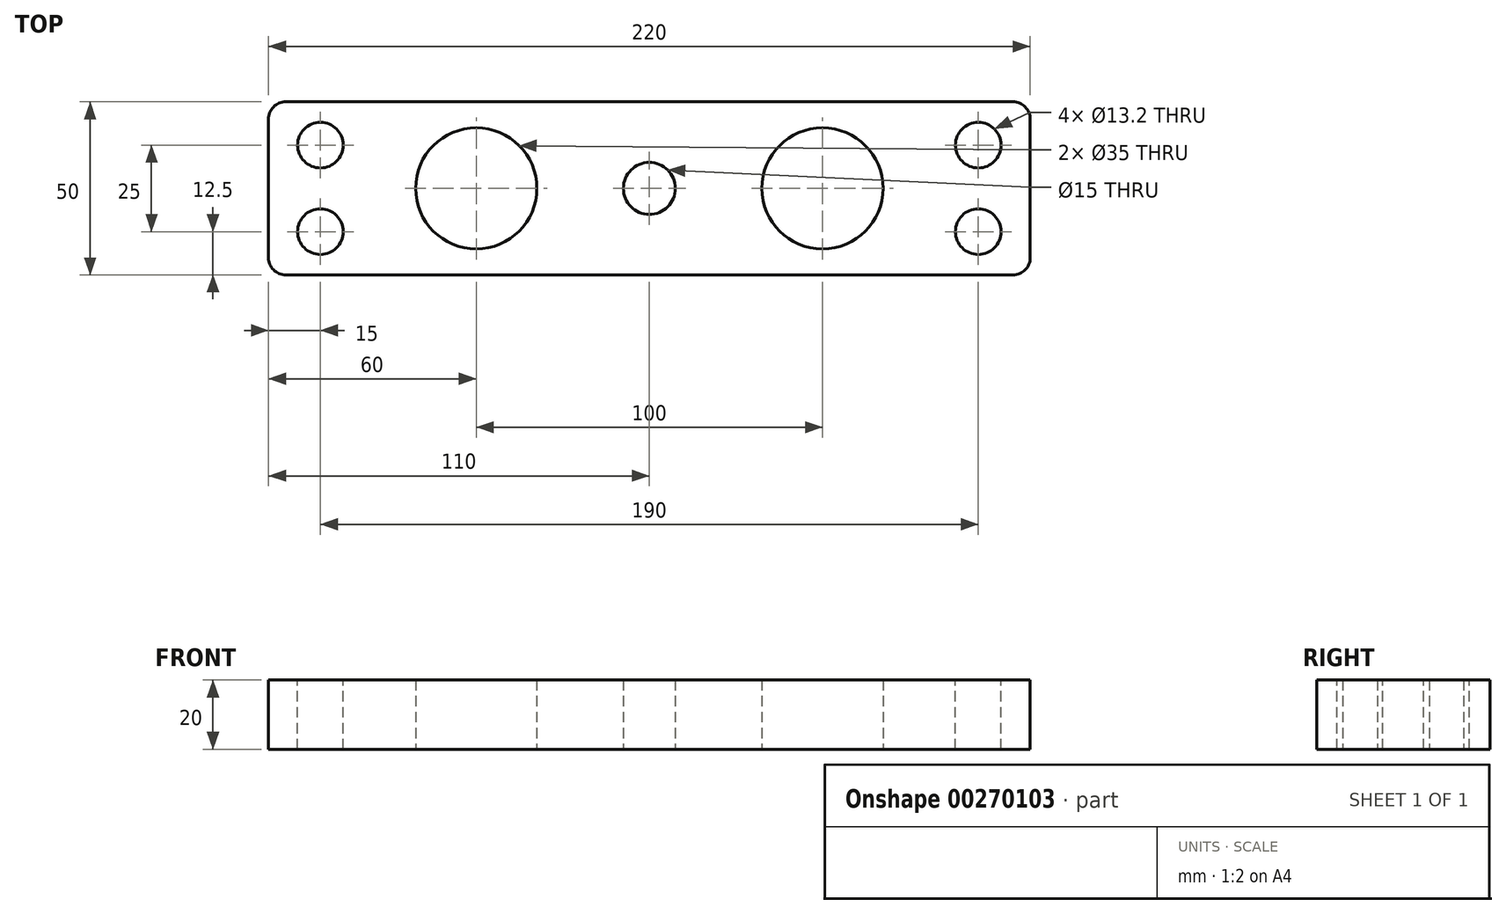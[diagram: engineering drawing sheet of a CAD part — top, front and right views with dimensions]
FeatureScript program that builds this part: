
annotation { "Feature Type Name" : "Feature", "Feature Type Description" : "" }
export const myFeature = defineFeature(function(context is Context, id is Id, definition is map)
    precondition{}
    {
        {
            var Q0;
            Q0=qCreatedBy(makeId("Top.planeOp"),FACE);
            var sketch = newSketch(context, id + "F0", { "sketchPlane" : qUnion([Q0])});
            skLineSegment(sketch, "E0.bottom", {"start": v(110, -25) * mm, "end": v(-110, -25) * mm});
            skLineSegment(sketch, "E0.top", {"start": v(110, 25) * mm, "end": v(-110, 25) * mm});
            skLineSegment(sketch, "E0.left", {"start": v(110, -25) * mm, "end": v(110, 25) * mm});
            skLineSegment(sketch, "E0.right", {"start": v(-110, -25) * mm, "end": v(-110, 25) * mm});
            skPoint(sketch, "E0.middle", {"position": v(0, 0) * mm});
            skPoint(sketch, "E1", {"position": v(-50, 0) * mm});
            skPoint(sketch, "E2", {"position": v(50, 0) * mm});
            skCircle(sketch, "E3", {"center": v(50, 0) * mm, "radius": 17.5 * mm});
            skCircle(sketch, "E4", {"center": v(-50, 0) * mm, "radius": 17.5 * mm});
            skCircle(sketch, "E5", {"center": v(0, 0) * mm, "radius": 7.5 * mm});
            skPoint(sketch, "E6", {"position": v(-95, 12.5) * mm});
            skPoint(sketch, "E7", {"position": v(-95, -12.5) * mm});
            skPoint(sketch, "E8", {"position": v(95, 12.5) * mm});
            skPoint(sketch, "E9", {"position": v(95, -12.5) * mm});
            skSolve(sketch);
        }
        {
            var Q0;
            Q0=makeQuery(id+"F0.imprint","IMPRINT",FACE,{"disambiguationData":[TD([[makeQuery(id+"F0.imprint","IMPRINT",EDGE,{"derivedFrom":sQuery(id+"F0.wireOp",EDGE,"E0.bottom")}),-1.0]])]});
            extrude(context, id + "F1", {"entities" : qUnion([Q0]), "depth" : 20 * mm});
        }
        {
            var Q0;
            Q0=sQuery(id+"F0.wireOp",VERTEX,"E6");
            var Q1;
            Q1=sQuery(id+"F0.wireOp",VERTEX,"E7");
            var Q2;
            Q2=sQuery(id+"F0.wireOp",VERTEX,"E8");
            var Q3;
            Q3=sQuery(id+"F0.wireOp",VERTEX,"E9");
            var Q4;
            Q4=makeQuery(id+"F1.opExtrude","SWEPT_BODY",BODY,{"disambiguationData":[OSD([sQuery(id+"F0.wireOp",EDGE,"E0.bottom"),sQuery(id+"F0.wireOp",EDGE,"E0.top"),sQuery(id+"F0.wireOp",EDGE,"E0.left"),sQuery(id+"F0.wireOp",EDGE,"E0.right"),sQuery(id+"F0.wireOp",EDGE,"E3"),sQuery(id+"F0.wireOp",EDGE,"E4"),sQuery(id+"F0.wireOp",EDGE,"E5")])]});
            hole(context, id + "F2", {"style" : HoleStyle.SIMPLE, "endStyle" : HoleEndStyle.THROUGH, "oppositeDirection" : true, "standardTappedOrClearance" : lookupTablePath({ "standard" : "ISO", "fit" : "Normal", "size" : "M12", "type" : "Clearance" }), "standardBlindInLast" : lookupTablePath({ "fit" : "Standard", "standard" : "ISO", "size" : "M12", "type" : "Clearance" }), "holeDiameter" : 13.2 * mm, "tappedDepth" : 60 * mm, "tapClearance" : 3, "startFromSketch" : true, "locations" : qUnion([Q0, Q1, Q2, Q3]), "scope" : qUnion([Q4])});
        }
        {
            var Q0;
            Q0=makeQuery(id+"F1.opExtrude","SWEPT_EDGE",EDGE,{"disambiguationData":[OSD([sQuery(id+"F0.wireOp",EDGE,"E0.bottom"),sQuery(id+"F0.wireOp",EDGE,"E0.right")])]});
            var Q1;
            Q1=makeQuery(id+"F1.opExtrude","SWEPT_EDGE",EDGE,{"disambiguationData":[OSD([sQuery(id+"F0.wireOp",EDGE,"E0.bottom"),sQuery(id+"F0.wireOp",EDGE,"E0.left")])]});
            var Q2;
            Q2=makeQuery(id+"F1.opExtrude","SWEPT_EDGE",EDGE,{"disambiguationData":[OSD([sQuery(id+"F0.wireOp",EDGE,"E0.top"),sQuery(id+"F0.wireOp",EDGE,"E0.left")])]});
            var Q3;
            Q3=makeQuery(id+"F1.opExtrude","SWEPT_EDGE",EDGE,{"disambiguationData":[OSD([sQuery(id+"F0.wireOp",EDGE,"E0.top"),sQuery(id+"F0.wireOp",EDGE,"E0.right")])]});
            fillet(context, id + "F3", {"entities" : qUnion([Q0, Q1, Q2, Q3]), "radius" : 5 * mm, "tangentPropagation" : true, "allowEdgeOverflow" : false});
        }
    });
